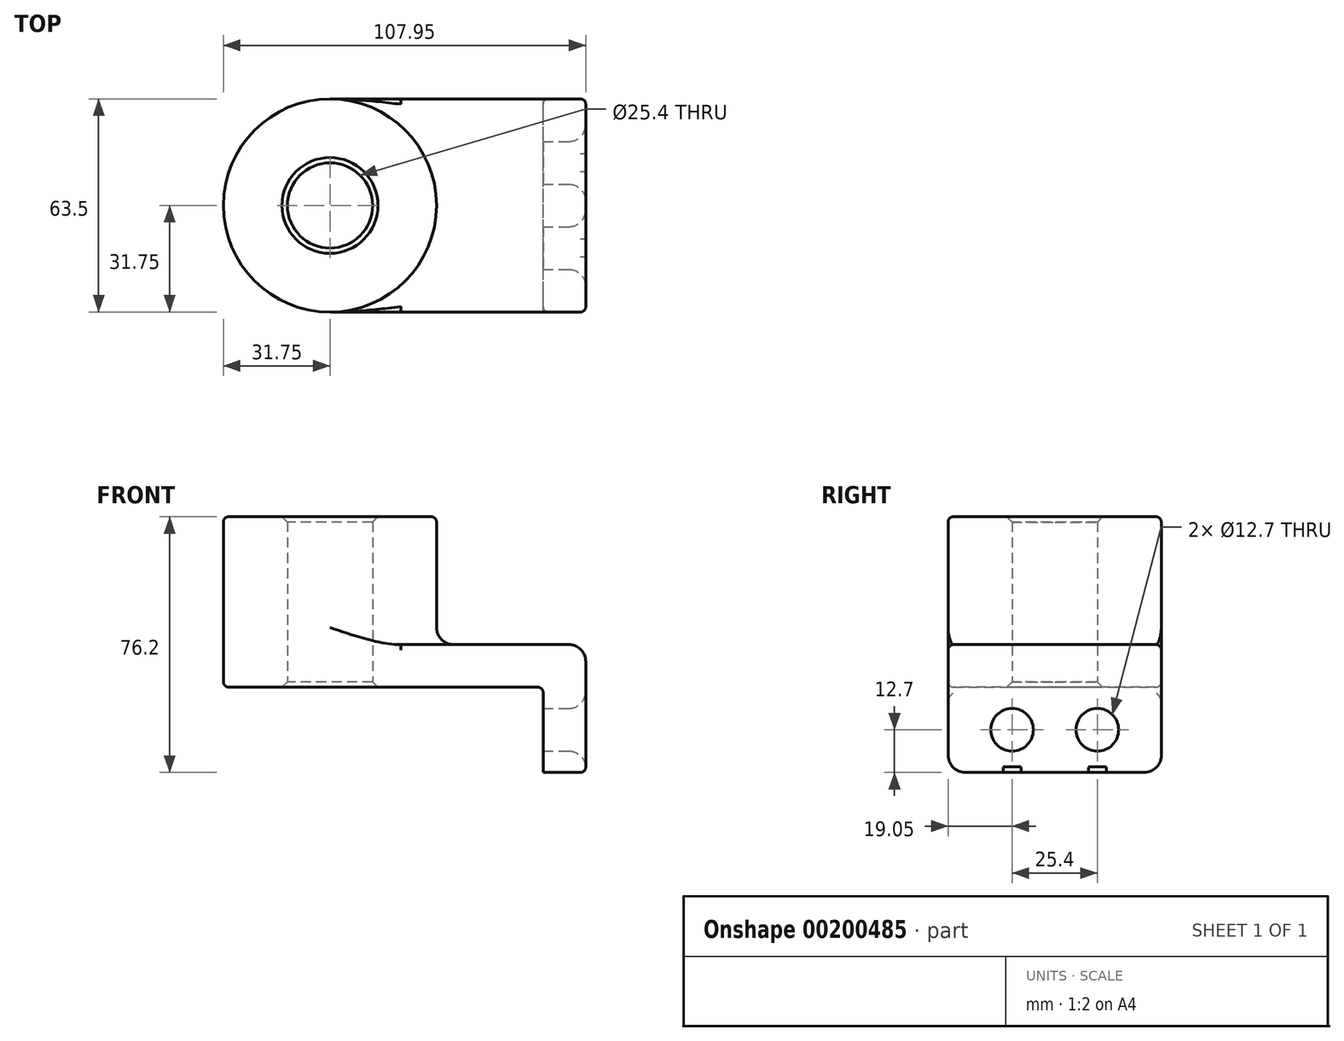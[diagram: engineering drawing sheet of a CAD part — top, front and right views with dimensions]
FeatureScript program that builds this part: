
annotation { "Feature Type Name" : "Feature", "Feature Type Description" : "" }
export const myFeature = defineFeature(function(context is Context, id is Id, definition is map)
    precondition{}
    {
        {
            var Q0;
            Q0=qCreatedBy(makeId("Top.planeOp"),FACE);
            var sketch = newSketch(context, id + "F0", { "sketchPlane" : qUnion([Q0])});
            skLineSegment(sketch, "E0.bottom", {"start": v(38.1, -31.75) * mm, "end": v(-38.1, -31.75) * mm});
            skLineSegment(sketch, "E0.top", {"start": v(38.1, 31.75) * mm, "end": v(-38.1, 31.75) * mm});
            skLineSegment(sketch, "E0.left", {"start": v(38.1, -31.75) * mm, "end": v(38.1, 31.75) * mm});
            skLineSegment(sketch, "E0.right", {"start": v(-38.1, -31.75) * mm, "end": v(-38.1, 31.75) * mm});
            skPoint(sketch, "E0.middle", {"position": v(0, 0) * mm});
            skCircle(sketch, "E1", {"center": v(-38.1, 0) * mm, "radius": 31.75 * mm});
            skCircle(sketch, "E2", {"center": v(-38.1, 0) * mm, "radius": 12.7 * mm});
            skSolve(sketch);
        }
        {
            var Q0;
            Q0 = qSketchRegion(id + "F0", true);
            extrude(context, id + "F1", {"entities" : qUnion([Q0]), "depth" : 12.7 * mm});
        }
        {
            var Q0;
            {var subQ1=sQuery(id+"F0.wireOp",EDGE,"E0.right");var subQ3=sQuery(id+"F0.wireOp",EDGE,"E2");var subQ4=makeQuery(id+"F0.imprint","INTERSECT",VERTEX,{"disambiguationData":[OD(0.0)],"derivedFrom":[subQ1,subQ3]});Q0=makeQuery(id+"F0.imprint","IMPRINT",FACE,{"disambiguationData":[TD([[makeQuery(id+"F0.imprint","IMPRINT",EDGE,{"disambiguationData":[TD([[subQ4,1.0]])],"derivedFrom":subQ3}),-1.0]])]});}
            var Q1;
            {var subQ1=sQuery(id+"F0.wireOp",EDGE,"E0.right");var subQ3=sQuery(id+"F0.wireOp",EDGE,"E2");var subQ4=makeQuery(id+"F0.imprint","INTERSECT",VERTEX,{"disambiguationData":[OD(0.0)],"derivedFrom":[subQ1,subQ3]});Q1=makeQuery(id+"F0.imprint","IMPRINT",FACE,{"disambiguationData":[TD([[makeQuery(id+"F0.imprint","IMPRINT",EDGE,{"disambiguationData":[TD([[subQ4,-1.0]])],"derivedFrom":subQ3}),-1.0]])]});}
            extrude(context, id + "F2", {"entities" : qUnion([Q0, Q1]), "operationType" : NewBodyOperationType.ADD, "depth" : 50.8 * mm});
        }
        {
            var Q0;
            Q0=makeQuery(id+"F1.opExtrude","SWEPT_FACE",FACE,{"disambiguationData":[OSD([sQuery(id+"F0.wireOp",EDGE,"E0.left")])]});
            var sketch = newSketch(context, id + "F3", { "sketchPlane" : qUnion([Q0])});
            skLineSegment(sketch, "E3.bottom", {"start": v(-31.75, 12.7) * mm, "end": v(31.75, 12.7) * mm});
            skLineSegment(sketch, "E3.top", {"start": v(-31.75, -25.4) * mm, "end": v(31.75, -25.4) * mm});
            skLineSegment(sketch, "E3.left", {"start": v(-31.75, 12.7) * mm, "end": v(-31.75, -25.4) * mm});
            skLineSegment(sketch, "E3.right", {"start": v(31.75, 12.7) * mm, "end": v(31.75, -25.4) * mm});
            skCircle(sketch, "E4", {"center": v(-12.7, -12.7) * mm, "radius": 6.35 * mm});
            skLineSegment(sketch, "E5", {"start": v(0, 0) * mm, "end": v(0, -25.4) * mm, "construction": true});
            skCircle(sketch, "E6.MirrorC", {"center": v(12.7, -12.7) * mm, "radius": 6.35 * mm});
            skSolve(sketch);
        }
        {
            var Q0;
            Q0 = qSketchRegion(id + "F3", true);
            extrude(context, id + "F4", {"entities" : qUnion([Q0]), "operationType" : NewBodyOperationType.ADD, "oppositeDirection" : true, "depth" : 12.7 * mm});
        }
        {
            var Q0;
            {var subQ0=sQuery(id+"F0.wireOp",EDGE,"E1");Q0=makeQuery(id+"F2.boolean.opBoolean","INTERSECT",EDGE,{"derivedFrom":[makeQuery(id+"F1.opExtrude","CAP_FACE",FACE,{"disambiguationData":[OSD([sQuery(id+"F0.wireOp",EDGE,"E0.bottom"),sQuery(id+"F0.wireOp",EDGE,"E0.top"),sQuery(id+"F0.wireOp",EDGE,"E0.left"),subQ0,sQuery(id+"F0.wireOp",EDGE,"E2")])],"isStart":false}),makeQuery(id+"F2.opExtrude","SWEPT_FACE",FACE,{"disambiguationData":[OSD([subQ0])]})]});}
            var Q1;
            Q1=makeQuery(id+"F1.opExtrude","CAP_EDGE",EDGE,{"disambiguationData":[OSD([sQuery(id+"F0.wireOp",EDGE,"E0.left")])],"isStart":false});
            var Q2;
            Q2=makeQuery(id+"F4.opExtrude","SWEPT_EDGE",EDGE,{"disambiguationData":[OSD([sQuery(id+"F3.wireOp",EDGE,"E3.top"),sQuery(id+"F3.wireOp",EDGE,"E3.left")])]});
            var Q3;
            Q3=makeQuery(id+"F4.opExtrude","CAP_EDGE",EDGE,{"disambiguationData":[OSD([sQuery(id+"F3.wireOp",EDGE,"E4")])],"isStart":true});
            var Q4;
            Q4=makeQuery(id+"F4.opExtrude","CAP_EDGE",EDGE,{"disambiguationData":[OSD([sQuery(id+"F3.wireOp",EDGE,"E6.MirrorC")])],"isStart":true});
            var Q5;
            Q5=makeQuery(id+"F4.opExtrude","SWEPT_EDGE",EDGE,{"disambiguationData":[OSD([sQuery(id+"F3.wireOp",EDGE,"E3.top"),sQuery(id+"F3.wireOp",EDGE,"E3.right")])]});
            fillet(context, id + "F5", {"entities" : qUnion([Q0, Q1, Q2, Q3, Q4, Q5]), "radius" : 5.08 * mm, "tangentPropagation" : true, "allowEdgeOverflow" : false});
        }
        {
            var Q0;
            Q0=makeQuery(id+"F1.opExtrude","CAP_EDGE",EDGE,{"disambiguationData":[OSD([sQuery(id+"F0.wireOp",EDGE,"E0.bottom")])],"isStart":false});
            var Q1;
            Q1=makeQuery(id+"F1.opExtrude","CAP_EDGE",EDGE,{"disambiguationData":[OSD([sQuery(id+"F0.wireOp",EDGE,"E0.bottom")])],"isStart":true});
            var Q2;
            Q2=makeQuery(id+"F4.boolean.opBoolean","INTERSECT",EDGE,{"derivedFrom":[makeQuery(id+"F1.opExtrude","CAP_FACE",FACE,{"disambiguationData":[OSD([sQuery(id+"F0.wireOp",EDGE,"E0.bottom"),sQuery(id+"F0.wireOp",EDGE,"E0.top"),sQuery(id+"F0.wireOp",EDGE,"E0.left"),sQuery(id+"F0.wireOp",EDGE,"E1"),sQuery(id+"F0.wireOp",EDGE,"E2")])],"isStart":true}),makeQuery(id+"F4.opExtrude","CAP_FACE",FACE,{"disambiguationData":[OSD([sQuery(id+"F3.wireOp",EDGE,"E3.bottom"),sQuery(id+"F3.wireOp",EDGE,"E3.top"),sQuery(id+"F3.wireOp",EDGE,"E3.left"),sQuery(id+"F3.wireOp",EDGE,"E3.right"),sQuery(id+"F3.wireOp",EDGE,"E4"),sQuery(id+"F3.wireOp",EDGE,"E6.MirrorC")])],"isStart":false})]});
            fillet(context, id + "F6", {"entities" : qUnion([Q0, Q1, Q2]), "radius" : 1.59 * mm, "tangentPropagation" : true, "allowEdgeOverflow" : false});
        }
        {
            var Q0;
            {var subQ0=sQuery(id+"F0.wireOp",EDGE,"E2");Q0=makeQuery(id+"F2.boolean.opBoolean","MERGE",FACE,{"derivedFrom":[makeQuery(id+"F1.opExtrude","SWEPT_FACE",FACE,{"disambiguationData":[OSD([subQ0])]}),makeQuery(id+"F2.opExtrude","SWEPT_FACE",FACE,{"disambiguationData":[OSD([subQ0])]})]});}
            chamfer(context, id + "F7", {"entities" : qUnion([Q0]), "width" : 1.59 * mm, "tangentPropagation" : true});
        }
        {
            var Q0;
            Q0=makeQuery(id+"F2.opExtrude","CAP_EDGE",EDGE,{"disambiguationData":[OSD([sQuery(id+"F0.wireOp",EDGE,"E1")])],"isStart":false});
            fillet(context, id + "F8", {"entities" : qUnion([Q0]), "radius" : 1.59 * mm, "tangentPropagation" : true, "allowEdgeOverflow" : false});
        }
    });
